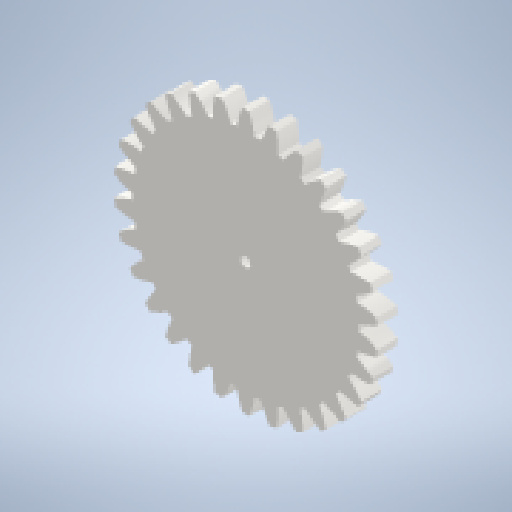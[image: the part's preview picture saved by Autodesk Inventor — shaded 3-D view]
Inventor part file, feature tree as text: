
AUTODESK INVENTOR PART (.ipt)
format: ipt  version: 2024 (Build 280153000, 153)  size: 285,696 bytes
history: native  units: mm (DEFAULTED — no unit token found)
features: plane x3, other x3, extrude x2, sketch x2
ambient origin geometry x8: Origin, YZ Plane, XZ Plane, XY Plane, X Axis, Y Axis, Z Axis, Center Point
bodies: Solid1 (feature_tree)
feature tree (10):
  extrude  "Extrusion1"  Depth=5.0mm TaperAngle=0.0deg
  plane  "Work Plane2"
  plane  "Work Plane8"
  plane  "Work Plane9"
  other  "Spur Gear"
  extrude  "Extrusion2"  Depth=10.0mm TaperAngle=0.0deg
  sketch  "Sketch1"  dims[d0=64.0mm d1=5.0mm d2=0.0mm]
  other  "Srf1"
  sketch  "Sketch3"  dims[d3=60.0mm d4=10.0mm d5=0.0mm d16=120.0mm d17=0.0mm d34=1.047198mm d39=0.0mm d41=0.0mm d43=120.0mm d46=120.0mm d47=0.0mm d48=0.0mm d49=2.5mm d50=10.0mm d51=0.0mm]
  other  "Pitch Diameter"
